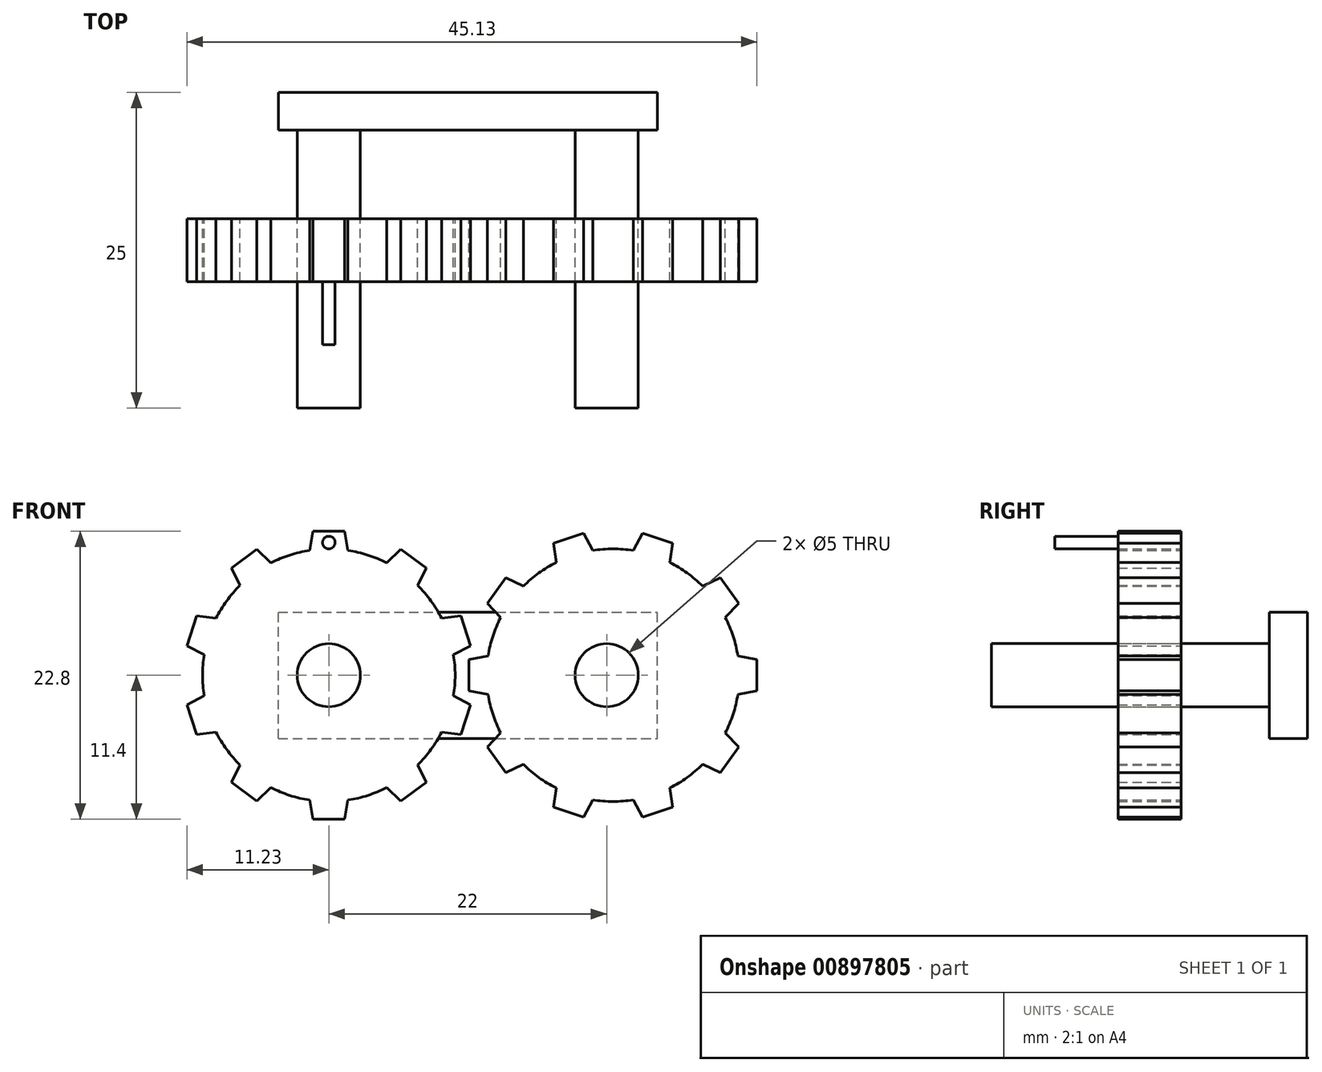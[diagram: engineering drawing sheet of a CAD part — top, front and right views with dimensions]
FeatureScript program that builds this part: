
annotation { "Feature Type Name" : "Feature", "Feature Type Description" : "" }
export const myFeature = defineFeature(function(context is Context, id is Id, definition is map)
    precondition{}
    {
        {
            var Q0;
            Q0=qCreatedBy(makeId("Front.planeOp"),FACE);
            var sketch = newSketch(context, id + "F0", { "sketchPlane" : qUnion([Q0])});
            skCircle(sketch, "E0", {"center": v(0, 0) * mm, "radius": 10 * mm});
            skLineSegment(sketch, "E1", {"start": v(0, 11.4) * mm, "end": v(1.25, 11.4) * mm});
            skLineSegment(sketch, "E2", {"start": v(1.25, 11.4) * mm, "end": v(1.52, 9.88) * mm});
            skLineSegment(sketch, "E3.MirrorCS", {"start": v(0, 11.4) * mm, "end": v(-1.25, 11.4) * mm});
            skLineSegment(sketch, "E4.MirrorCS", {"start": v(-1.25, 11.4) * mm, "end": v(-1.52, 9.88) * mm});
            skLineSegment(sketch, "E5.1.0", {"start": v(-5.69, 9.96) * mm, "end": v(-4.58, 8.89) * mm});
            skLineSegment(sketch, "E5.1.1", {"start": v(-6.7, 9.22) * mm, "end": v(-5.69, 9.96) * mm});
            skLineSegment(sketch, "E5.1.2", {"start": v(-6.7, 9.22) * mm, "end": v(-7.71, 8.49) * mm});
            skLineSegment(sketch, "E5.1.3", {"start": v(-7.71, 8.49) * mm, "end": v(-7.04, 7.1) * mm});
            skLineSegment(sketch, "E5.2.0", {"start": v(-10.46, 4.71) * mm, "end": v(-8.93, 4.5) * mm});
            skLineSegment(sketch, "E5.2.1", {"start": v(-10.84, 3.52) * mm, "end": v(-10.46, 4.71) * mm});
            skLineSegment(sketch, "E5.2.2", {"start": v(-10.84, 3.52) * mm, "end": v(-11.23, 2.33) * mm});
            skLineSegment(sketch, "E5.2.3", {"start": v(-11.23, 2.33) * mm, "end": v(-9.87, 1.61) * mm});
            skLineSegment(sketch, "E6.2.3.0", {"start": v(-11.23, -2.33) * mm, "end": v(-9.87, -1.61) * mm});
            skLineSegment(sketch, "E6.3.3.0", {"start": v(-10.84, -3.52) * mm, "end": v(-11.23, -2.33) * mm});
            skLineSegment(sketch, "E6.6.3.0", {"start": v(-10.84, -3.52) * mm, "end": v(-10.46, -4.71) * mm});
            skLineSegment(sketch, "E6.9.3.0", {"start": v(-10.46, -4.71) * mm, "end": v(-8.93, -4.5) * mm});
            skLineSegment(sketch, "E6.2.4.0", {"start": v(-7.71, -8.49) * mm, "end": v(-7.04, -7.1) * mm});
            skLineSegment(sketch, "E6.3.4.0", {"start": v(-6.7, -9.22) * mm, "end": v(-7.71, -8.49) * mm});
            skLineSegment(sketch, "E6.6.4.0", {"start": v(-6.7, -9.22) * mm, "end": v(-5.69, -9.96) * mm});
            skLineSegment(sketch, "E6.9.4.0", {"start": v(-5.69, -9.96) * mm, "end": v(-4.58, -8.89) * mm});
            skLineSegment(sketch, "E6.2.5.0", {"start": v(-1.25, -11.4) * mm, "end": v(-1.52, -9.88) * mm});
            skLineSegment(sketch, "E6.3.5.0", {"start": v(0, -11.4) * mm, "end": v(-1.25, -11.4) * mm});
            skLineSegment(sketch, "E6.6.5.0", {"start": v(0, -11.4) * mm, "end": v(1.25, -11.4) * mm});
            skLineSegment(sketch, "E6.9.5.0", {"start": v(1.25, -11.4) * mm, "end": v(1.52, -9.88) * mm});
            skLineSegment(sketch, "E7.2.6.0", {"start": v(5.69, -9.96) * mm, "end": v(4.58, -8.89) * mm});
            skLineSegment(sketch, "E7.3.6.0", {"start": v(6.7, -9.22) * mm, "end": v(5.69, -9.96) * mm});
            skLineSegment(sketch, "E7.6.6.0", {"start": v(6.7, -9.22) * mm, "end": v(7.71, -8.49) * mm});
            skLineSegment(sketch, "E7.9.6.0", {"start": v(7.71, -8.49) * mm, "end": v(7.04, -7.1) * mm});
            skLineSegment(sketch, "E7.2.7.0", {"start": v(10.46, -4.71) * mm, "end": v(8.93, -4.5) * mm});
            skLineSegment(sketch, "E7.3.7.0", {"start": v(10.84, -3.52) * mm, "end": v(10.46, -4.71) * mm});
            skLineSegment(sketch, "E7.6.7.0", {"start": v(10.84, -3.52) * mm, "end": v(11.23, -2.33) * mm});
            skLineSegment(sketch, "E7.9.7.0", {"start": v(11.23, -2.33) * mm, "end": v(9.87, -1.61) * mm});
            skLineSegment(sketch, "E7.2.8.0", {"start": v(11.23, 2.33) * mm, "end": v(9.87, 1.61) * mm});
            skLineSegment(sketch, "E7.3.8.0", {"start": v(10.84, 3.52) * mm, "end": v(11.23, 2.33) * mm});
            skLineSegment(sketch, "E7.6.8.0", {"start": v(10.84, 3.52) * mm, "end": v(10.46, 4.71) * mm});
            skLineSegment(sketch, "E7.9.8.0", {"start": v(10.46, 4.71) * mm, "end": v(8.93, 4.5) * mm});
            skLineSegment(sketch, "E7.2.9.0", {"start": v(7.71, 8.49) * mm, "end": v(7.04, 7.1) * mm});
            skLineSegment(sketch, "E7.3.9.0", {"start": v(6.7, 9.22) * mm, "end": v(7.71, 8.49) * mm});
            skLineSegment(sketch, "E7.6.9.0", {"start": v(6.7, 9.22) * mm, "end": v(5.69, 9.96) * mm});
            skLineSegment(sketch, "E7.9.9.0", {"start": v(5.69, 9.96) * mm, "end": v(4.58, 8.89) * mm});
            skPoint(sketch, "E8", {"position": v(0, 10.7) * mm});
            skSolve(sketch);
        }
        {
            var Q0;
            Q0 = qSketchRegion(id + "F0", true);
            extrude(context, id + "F1", {"entities" : qUnion([Q0]), "depth" : 5 * mm, "offsetDistance" : 25 * mm});
        }
        {
            var Q0;
            Q0=qCreatedBy(makeId("Front.planeOp"),FACE);
            var sketch = newSketch(context, id + "F2", { "sketchPlane" : qUnion([Q0])});
            skLineSegment(sketch, "E9", {"start": v(0, 0) * mm, "end": v(22.5, 0) * mm});
            skCircle(sketch, "E10", {"center": v(22.5, 0) * mm, "radius": 10 * mm});
            skLineSegment(sketch, "E11", {"start": v(11.1, 0) * mm, "end": v(11.1, -1.25) * mm});
            skLineSegment(sketch, "E12", {"start": v(11.1, -1.25) * mm, "end": v(12.62, -1.52) * mm});
            skLineSegment(sketch, "E13.MirrorCS", {"start": v(11.1, 0) * mm, "end": v(11.1, 1.25) * mm});
            skLineSegment(sketch, "E14.MirrorCS", {"start": v(11.1, 1.25) * mm, "end": v(12.62, 1.52) * mm});
            skLineSegment(sketch, "E15.1.0", {"start": v(12.54, -5.69) * mm, "end": v(13.61, -4.58) * mm});
            skLineSegment(sketch, "E15.1.1", {"start": v(13.28, -6.7) * mm, "end": v(12.54, -5.69) * mm});
            skLineSegment(sketch, "E15.1.2", {"start": v(13.28, -6.7) * mm, "end": v(14.01, -7.71) * mm});
            skLineSegment(sketch, "E15.1.3", {"start": v(14.01, -7.71) * mm, "end": v(15.4, -7.04) * mm});
            skLineSegment(sketch, "E15.2.0", {"start": v(17.79, -10.46) * mm, "end": v(18, -8.93) * mm});
            skLineSegment(sketch, "E15.2.1", {"start": v(18.98, -10.84) * mm, "end": v(17.79, -10.46) * mm});
            skLineSegment(sketch, "E15.2.2", {"start": v(18.98, -10.84) * mm, "end": v(20.17, -11.23) * mm});
            skLineSegment(sketch, "E15.2.3", {"start": v(20.17, -11.23) * mm, "end": v(20.89, -9.87) * mm});
            skLineSegment(sketch, "E15.3.0", {"start": v(24.83, -11.23) * mm, "end": v(24.11, -9.87) * mm});
            skLineSegment(sketch, "E15.3.1", {"start": v(26.02, -10.84) * mm, "end": v(24.83, -11.23) * mm});
            skLineSegment(sketch, "E15.3.2", {"start": v(26.02, -10.84) * mm, "end": v(27.21, -10.46) * mm});
            skLineSegment(sketch, "E15.3.3", {"start": v(27.21, -10.46) * mm, "end": v(27, -8.93) * mm});
            skLineSegment(sketch, "E15.4.0", {"start": v(30.99, -7.71) * mm, "end": v(29.6, -7.04) * mm});
            skLineSegment(sketch, "E15.4.1", {"start": v(31.72, -6.7) * mm, "end": v(30.99, -7.71) * mm});
            skLineSegment(sketch, "E15.4.2", {"start": v(31.72, -6.7) * mm, "end": v(32.46, -5.69) * mm});
            skLineSegment(sketch, "E15.4.3", {"start": v(32.46, -5.69) * mm, "end": v(31.39, -4.58) * mm});
            skLineSegment(sketch, "E15.5.0", {"start": v(33.9, -1.25) * mm, "end": v(32.38, -1.52) * mm});
            skLineSegment(sketch, "E15.5.1", {"start": v(33.9, 0) * mm, "end": v(33.9, -1.25) * mm});
            skLineSegment(sketch, "E15.5.2", {"start": v(33.9, 0) * mm, "end": v(33.9, 1.25) * mm});
            skLineSegment(sketch, "E15.5.3", {"start": v(33.9, 1.25) * mm, "end": v(32.38, 1.52) * mm});
            skLineSegment(sketch, "E15.6.0", {"start": v(32.46, 5.69) * mm, "end": v(31.39, 4.58) * mm});
            skLineSegment(sketch, "E15.6.1", {"start": v(31.72, 6.7) * mm, "end": v(32.46, 5.69) * mm});
            skLineSegment(sketch, "E15.6.2", {"start": v(31.72, 6.7) * mm, "end": v(30.99, 7.71) * mm});
            skLineSegment(sketch, "E15.6.3", {"start": v(30.99, 7.71) * mm, "end": v(29.6, 7.04) * mm});
            skLineSegment(sketch, "E15.7.0", {"start": v(27.21, 10.46) * mm, "end": v(27, 8.93) * mm});
            skLineSegment(sketch, "E15.7.1", {"start": v(26.02, 10.84) * mm, "end": v(27.21, 10.46) * mm});
            skLineSegment(sketch, "E15.7.2", {"start": v(26.02, 10.84) * mm, "end": v(24.83, 11.23) * mm});
            skLineSegment(sketch, "E15.7.3", {"start": v(24.83, 11.23) * mm, "end": v(24.11, 9.87) * mm});
            skLineSegment(sketch, "E16.1.8.0", {"start": v(20.17, 11.23) * mm, "end": v(20.89, 9.87) * mm});
            skLineSegment(sketch, "E16.3.8.0", {"start": v(18.98, 10.84) * mm, "end": v(20.17, 11.23) * mm});
            skLineSegment(sketch, "E16.6.8.0", {"start": v(18.98, 10.84) * mm, "end": v(17.79, 10.46) * mm});
            skLineSegment(sketch, "E16.9.8.0", {"start": v(17.79, 10.46) * mm, "end": v(18, 8.93) * mm});
            skLineSegment(sketch, "E17.1.9.0", {"start": v(14.01, 7.71) * mm, "end": v(15.4, 7.04) * mm});
            skLineSegment(sketch, "E17.3.9.0", {"start": v(13.28, 6.7) * mm, "end": v(14.01, 7.71) * mm});
            skLineSegment(sketch, "E17.6.9.0", {"start": v(13.28, 6.7) * mm, "end": v(12.54, 5.69) * mm});
            skLineSegment(sketch, "E17.9.9.0", {"start": v(12.54, 5.69) * mm, "end": v(13.61, 4.58) * mm});
            skSolve(sketch);
        }
        {
            var Q0;
            Q0 = qSketchRegion(id + "F2", true);
            extrude(context, id + "F3", {"entities" : qUnion([Q0]), "depth" : 5 * mm, "offsetDistance" : 25 * mm});
        }
        {
            var Q0;
            Q0=qCreatedBy(makeId("Front.planeOp"),FACE);
            cPlane(context, id + "F4", {"entities" : qUnion([Q0]), "cplaneType" : CPlaneType.OFFSET, "offset" : 10 * mm, "oppositeDirection" : true, "width" : 150 * mm, "height" : 150 * mm});
        }
        {
            var Q0;
            Q0=qCreatedBy(id+"F4.planeOp",FACE);
            var sketch = newSketch(context, id + "F5", { "sketchPlane" : qUnion([Q0])});
            skCircle(sketch, "E18", {"center": v(0, 0) * mm, "radius": 2.5 * mm});
            skSolve(sketch);
        }
        {
            var Q0;
            Q0 = qSketchRegion(id + "F5", true);
            extrude(context, id + "F6", {"entities" : qUnion([Q0]), "depth" : 25 * mm, "offsetDistance" : 25 * mm});
        }
        {
            var Q0;
            Q0=makeQuery(id+"F6.opExtrude","SWEPT_BODY",BODY,{"disambiguationData":[OSD([sQuery(id+"F5.wireOp",EDGE,"E18")])]});
            var Q1;
            Q1=makeQuery(id+"F1.opExtrude","SWEPT_BODY",BODY,{"disambiguationData":[OSD([sQuery(id+"F0.wireOp",EDGE,"E0"),sQuery(id+"F0.wireOp",EDGE,"E1"),sQuery(id+"F0.wireOp",EDGE,"E2"),sQuery(id+"F0.wireOp",EDGE,"E3.MirrorCS"),sQuery(id+"F0.wireOp",EDGE,"E4.MirrorCS"),sQuery(id+"F0.wireOp",EDGE,"E5.1.0"),sQuery(id+"F0.wireOp",EDGE,"E5.1.1"),sQuery(id+"F0.wireOp",EDGE,"E5.1.2"),sQuery(id+"F0.wireOp",EDGE,"E5.1.3"),sQuery(id+"F0.wireOp",EDGE,"E5.2.0"),sQuery(id+"F0.wireOp",EDGE,"E5.2.1"),sQuery(id+"F0.wireOp",EDGE,"E5.2.2"),sQuery(id+"F0.wireOp",EDGE,"E5.2.3"),sQuery(id+"F0.wireOp",EDGE,"E6.2.3.0"),sQuery(id+"F0.wireOp",EDGE,"E6.3.3.0"),sQuery(id+"F0.wireOp",EDGE,"E6.6.3.0"),sQuery(id+"F0.wireOp",EDGE,"E6.9.3.0"),sQuery(id+"F0.wireOp",EDGE,"E6.2.4.0"),sQuery(id+"F0.wireOp",EDGE,"E6.3.4.0"),sQuery(id+"F0.wireOp",EDGE,"E6.6.4.0"),sQuery(id+"F0.wireOp",EDGE,"E6.9.4.0"),sQuery(id+"F0.wireOp",EDGE,"E6.2.5.0"),sQuery(id+"F0.wireOp",EDGE,"E6.3.5.0"),sQuery(id+"F0.wireOp",EDGE,"E6.6.5.0"),sQuery(id+"F0.wireOp",EDGE,"E6.9.5.0"),sQuery(id+"F0.wireOp",EDGE,"E6.2.6.0"),sQuery(id+"F0.wireOp",EDGE,"E6.3.6.0"),sQuery(id+"F0.wireOp",EDGE,"E6.6.6.0"),sQuery(id+"F0.wireOp",EDGE,"E6.9.6.0"),sQuery(id+"F0.wireOp",EDGE,"E6.2.7.0"),sQuery(id+"F0.wireOp",EDGE,"E6.3.7.0"),sQuery(id+"F0.wireOp",EDGE,"E6.6.7.0"),sQuery(id+"F0.wireOp",EDGE,"E6.9.7.0"),sQuery(id+"F0.wireOp",EDGE,"E6.2.8.0"),sQuery(id+"F0.wireOp",EDGE,"E6.3.8.0"),sQuery(id+"F0.wireOp",EDGE,"E6.6.8.0"),sQuery(id+"F0.wireOp",EDGE,"E6.9.8.0"),sQuery(id+"F0.wireOp",EDGE,"E6.2.9.0"),sQuery(id+"F0.wireOp",EDGE,"E6.3.9.0"),sQuery(id+"F0.wireOp",EDGE,"E6.6.9.0"),sQuery(id+"F0.wireOp",EDGE,"E6.9.9.0")])]});
            booleanBodies(context, id + "F7", {"operationType" : BooleanOperationType.SUBTRACTION, "tools" : qUnion([Q0]), "targets" : qUnion([Q1]), "keepTools" : true});
        }
        {
            var Q0;
            Q0=qCreatedBy(id+"F4.planeOp",FACE);
            var sketch = newSketch(context, id + "F8", { "sketchPlane" : qUnion([Q0])});
            skLineSegment(sketch, "E19", {"start": v(0, 0) * mm, "end": v(22, 0) * mm});
            skCircle(sketch, "E20", {"center": v(22, 0) * mm, "radius": 2.5 * mm});
            skSolve(sketch);
        }
        {
            var Q0;
            Q0=makeQuery(id+"F8.imprint","IMPRINT",FACE,{"disambiguationData":[TD([[makeQuery(id+"F8.imprint","IMPRINT",EDGE,{"derivedFrom":sQuery(id+"F8.wireOp",EDGE,"E20")}),1.0]])]});
            extrude(context, id + "F9", {"entities" : qUnion([Q0]), "depth" : 25 * mm, "offsetDistance" : 25 * mm});
        }
        {
            var Q0;
            Q0=makeQuery(id+"F9.opExtrude","SWEPT_BODY",BODY,{"disambiguationData":[OSD([sQuery(id+"F8.wireOp",EDGE,"E20")])]});
            var Q1;
            Q1=makeQuery(id+"F3.opExtrude","SWEPT_BODY",BODY,{"disambiguationData":[OSD([sQuery(id+"F2.wireOp",EDGE,"E10"),sQuery(id+"F2.wireOp",EDGE,"E11"),sQuery(id+"F2.wireOp",EDGE,"E12"),sQuery(id+"F2.wireOp",EDGE,"E13.MirrorCS"),sQuery(id+"F2.wireOp",EDGE,"E14.MirrorCS"),sQuery(id+"F2.wireOp",EDGE,"E15.1.0"),sQuery(id+"F2.wireOp",EDGE,"E15.1.1"),sQuery(id+"F2.wireOp",EDGE,"E15.1.2"),sQuery(id+"F2.wireOp",EDGE,"E15.1.3"),sQuery(id+"F2.wireOp",EDGE,"E15.2.0"),sQuery(id+"F2.wireOp",EDGE,"E15.2.1"),sQuery(id+"F2.wireOp",EDGE,"E15.2.2"),sQuery(id+"F2.wireOp",EDGE,"E15.2.3"),sQuery(id+"F2.wireOp",EDGE,"E15.3.0"),sQuery(id+"F2.wireOp",EDGE,"E15.3.1"),sQuery(id+"F2.wireOp",EDGE,"E15.3.2"),sQuery(id+"F2.wireOp",EDGE,"E15.3.3"),sQuery(id+"F2.wireOp",EDGE,"E15.4.0"),sQuery(id+"F2.wireOp",EDGE,"E15.4.1"),sQuery(id+"F2.wireOp",EDGE,"E15.4.2"),sQuery(id+"F2.wireOp",EDGE,"E15.4.3"),sQuery(id+"F2.wireOp",EDGE,"E15.5.0"),sQuery(id+"F2.wireOp",EDGE,"E15.5.1"),sQuery(id+"F2.wireOp",EDGE,"E15.5.2"),sQuery(id+"F2.wireOp",EDGE,"E15.5.3"),sQuery(id+"F2.wireOp",EDGE,"E15.6.0"),sQuery(id+"F2.wireOp",EDGE,"E15.6.1"),sQuery(id+"F2.wireOp",EDGE,"E15.6.2"),sQuery(id+"F2.wireOp",EDGE,"E15.6.3"),sQuery(id+"F2.wireOp",EDGE,"E15.7.0"),sQuery(id+"F2.wireOp",EDGE,"E15.7.1"),sQuery(id+"F2.wireOp",EDGE,"E15.7.2"),sQuery(id+"F2.wireOp",EDGE,"E15.7.3"),sQuery(id+"F2.wireOp",EDGE,"E15.8.0"),sQuery(id+"F2.wireOp",EDGE,"E15.8.1"),sQuery(id+"F2.wireOp",EDGE,"E15.8.2"),sQuery(id+"F2.wireOp",EDGE,"E15.8.3"),sQuery(id+"F2.wireOp",EDGE,"E15.9.0"),sQuery(id+"F2.wireOp",EDGE,"E15.9.1"),sQuery(id+"F2.wireOp",EDGE,"E15.9.2"),sQuery(id+"F2.wireOp",EDGE,"E15.9.3")])]});
            booleanBodies(context, id + "F10", {"operationType" : BooleanOperationType.SUBTRACTION, "tools" : qUnion([Q0]), "targets" : qUnion([Q1]), "keepTools" : true});
        }
        {
            var Q0;
            Q0=qCreatedBy(id+"F4.planeOp",FACE);
            var sketch = newSketch(context, id + "F11", { "sketchPlane" : qUnion([Q0])});
            skLineSegment(sketch, "E21", {"start": v(0, 0) * mm, "end": v(11, 0) * mm});
            skLineSegment(sketch, "E22.bottom", {"start": v(-4, -5) * mm, "end": v(26, -5) * mm});
            skLineSegment(sketch, "E22.top", {"start": v(-4, 5) * mm, "end": v(26, 5) * mm});
            skLineSegment(sketch, "E22.left", {"start": v(-4, -5) * mm, "end": v(-4, 5) * mm});
            skLineSegment(sketch, "E22.right", {"start": v(26, -5) * mm, "end": v(26, 5) * mm});
            skPoint(sketch, "E22.middle", {"position": v(11, 0) * mm});
            skSolve(sketch);
        }
        {
            var Q0;
            Q0 = qSketchRegion(id + "F11", true);
            extrude(context, id + "F12", {"entities" : qUnion([Q0]), "operationType" : NewBodyOperationType.ADD, "depth" : 3 * mm, "offsetDistance" : 25 * mm});
        }
        {
            var Q0;
            Q0=makeQuery(id+"F1.opExtrude","CAP_FACE",FACE,{"disambiguationData":[OSD([sQuery(id+"F0.wireOp",EDGE,"E0"),sQuery(id+"F0.wireOp",EDGE,"E1"),sQuery(id+"F0.wireOp",EDGE,"E2"),sQuery(id+"F0.wireOp",EDGE,"E3.MirrorCS"),sQuery(id+"F0.wireOp",EDGE,"E4.MirrorCS"),sQuery(id+"F0.wireOp",EDGE,"E5.1.0"),sQuery(id+"F0.wireOp",EDGE,"E5.1.1"),sQuery(id+"F0.wireOp",EDGE,"E5.1.2"),sQuery(id+"F0.wireOp",EDGE,"E5.1.3"),sQuery(id+"F0.wireOp",EDGE,"E5.2.0"),sQuery(id+"F0.wireOp",EDGE,"E5.2.1"),sQuery(id+"F0.wireOp",EDGE,"E5.2.2"),sQuery(id+"F0.wireOp",EDGE,"E5.2.3"),sQuery(id+"F0.wireOp",EDGE,"E6.2.3.0"),sQuery(id+"F0.wireOp",EDGE,"E6.3.3.0"),sQuery(id+"F0.wireOp",EDGE,"E6.6.3.0"),sQuery(id+"F0.wireOp",EDGE,"E6.9.3.0"),sQuery(id+"F0.wireOp",EDGE,"E6.2.4.0"),sQuery(id+"F0.wireOp",EDGE,"E6.3.4.0"),sQuery(id+"F0.wireOp",EDGE,"E6.6.4.0"),sQuery(id+"F0.wireOp",EDGE,"E6.9.4.0"),sQuery(id+"F0.wireOp",EDGE,"E6.2.5.0"),sQuery(id+"F0.wireOp",EDGE,"E6.3.5.0"),sQuery(id+"F0.wireOp",EDGE,"E6.6.5.0"),sQuery(id+"F0.wireOp",EDGE,"E6.9.5.0"),sQuery(id+"F0.wireOp",EDGE,"E7.2.6.0"),sQuery(id+"F0.wireOp",EDGE,"E7.3.6.0"),sQuery(id+"F0.wireOp",EDGE,"E7.6.6.0"),sQuery(id+"F0.wireOp",EDGE,"E7.9.6.0"),sQuery(id+"F0.wireOp",EDGE,"E7.2.7.0"),sQuery(id+"F0.wireOp",EDGE,"E7.3.7.0"),sQuery(id+"F0.wireOp",EDGE,"E7.6.7.0"),sQuery(id+"F0.wireOp",EDGE,"E7.9.7.0"),sQuery(id+"F0.wireOp",EDGE,"E7.2.8.0"),sQuery(id+"F0.wireOp",EDGE,"E7.3.8.0"),sQuery(id+"F0.wireOp",EDGE,"E7.6.8.0"),sQuery(id+"F0.wireOp",EDGE,"E7.9.8.0"),sQuery(id+"F0.wireOp",EDGE,"E7.2.9.0"),sQuery(id+"F0.wireOp",EDGE,"E7.3.9.0"),sQuery(id+"F0.wireOp",EDGE,"E7.6.9.0"),sQuery(id+"F0.wireOp",EDGE,"E7.9.9.0")])],"isStart":false});
            var sketch = newSketch(context, id + "F13", { "sketchPlane" : qUnion([Q0])});
            skCircle(sketch, "E23", {"center": v(0, 10.5) * mm, "radius": 0.5 * mm});
            skSolve(sketch);
        }
        {
            var Q0;
            Q0=makeQuery(id+"F13.imprint","IMPRINT",FACE,{"disambiguationData":[TD([[makeQuery(id+"F13.imprint","IMPRINT",EDGE,{"derivedFrom":sQuery(id+"F13.wireOp",EDGE,"E23")}),1.0]])]});
            extrude(context, id + "F14", {"entities" : qUnion([Q0]), "depth" : 5 * mm, "offsetDistance" : 25 * mm});
        }
    });
